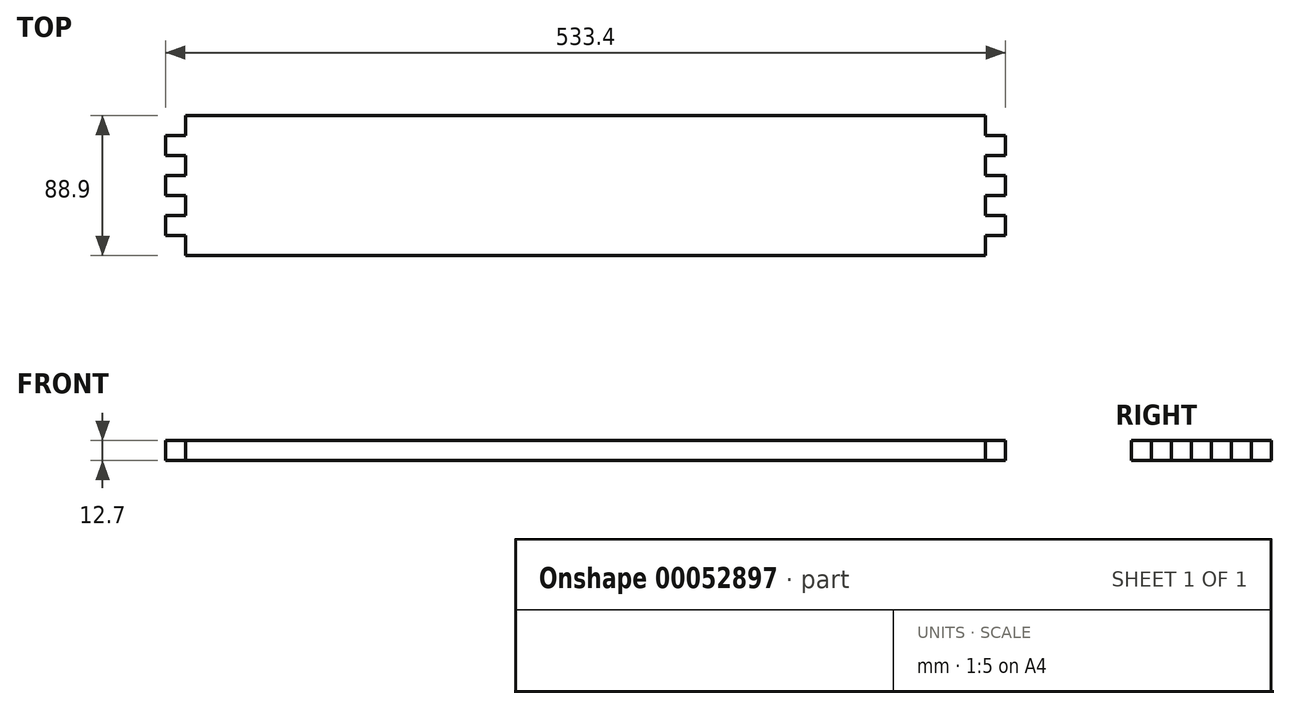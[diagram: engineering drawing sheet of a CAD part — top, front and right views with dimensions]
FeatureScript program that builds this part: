
annotation { "Feature Type Name" : "Feature", "Feature Type Description" : "" }
export const myFeature = defineFeature(function(context is Context, id is Id, definition is map)
    precondition{}
    {
        {
            var Q0;
            Q0=qCreatedBy(makeId("Top.planeOp"),FACE);
            var sketch = newSketch(context, id + "F0", { "sketchPlane" : qUnion([Q0])});
            skLineSegment(sketch, "E0.bottom", {"start": v(0, 0) * mm, "end": v(533.4, 0) * mm});
            skLineSegment(sketch, "E0.top", {"start": v(0, 88.9) * mm, "end": v(533.4, 88.9) * mm});
            skLineSegment(sketch, "E0.left", {"start": v(0, 0) * mm, "end": v(0, 88.9) * mm});
            skLineSegment(sketch, "E0.right", {"start": v(533.4, 0) * mm, "end": v(533.4, 88.9) * mm});
            skSolve(sketch);
        }
        {
            var Q0;
            Q0=qSketchRegion(id+"F0",true);
            extrude(context, id + "F1", {"entities" : qUnion([Q0]), "depth" : 12.7 * mm});
        }
        {
            var Q0;
            Q0=makeQuery(id+"F1.opExtrude","CAP_FACE",FACE,{"disambiguationData":[OSD([sQuery(id+"F0.wireOp",EDGE,"E0.bottom"),sQuery(id+"F0.wireOp",EDGE,"E0.top"),sQuery(id+"F0.wireOp",EDGE,"E0.left"),sQuery(id+"F0.wireOp",EDGE,"E0.right")])],"isStart":false});
            var sketch = newSketch(context, id + "F2", { "sketchPlane" : qUnion([Q0])});
            skLineSegment(sketch, "E1.bottom", {"start": v(533.4, 0) * mm, "end": v(520.7, 0) * mm});
            skLineSegment(sketch, "E1.top", {"start": v(533.4, 12.7) * mm, "end": v(520.7, 12.7) * mm});
            skLineSegment(sketch, "E1.left", {"start": v(533.4, 0) * mm, "end": v(533.4, 12.7) * mm});
            skLineSegment(sketch, "E1.right", {"start": v(520.7, 0) * mm, "end": v(520.7, 12.7) * mm});
            skLineSegment(sketch, "E2.bottom", {"start": v(533.4, 25.4) * mm, "end": v(520.7, 25.4) * mm});
            skLineSegment(sketch, "E2.top", {"start": v(533.4, 38.1) * mm, "end": v(520.7, 38.1) * mm});
            skLineSegment(sketch, "E2.left", {"start": v(533.4, 25.4) * mm, "end": v(533.4, 38.1) * mm});
            skLineSegment(sketch, "E2.right", {"start": v(520.7, 25.4) * mm, "end": v(520.7, 38.1) * mm});
            skLineSegment(sketch, "E3.bottom", {"start": v(533.4, 50.8) * mm, "end": v(520.7, 50.8) * mm});
            skLineSegment(sketch, "E3.top", {"start": v(533.4, 63.5) * mm, "end": v(520.7, 63.5) * mm});
            skLineSegment(sketch, "E3.left", {"start": v(533.4, 50.8) * mm, "end": v(533.4, 63.5) * mm});
            skLineSegment(sketch, "E3.right", {"start": v(520.7, 50.8) * mm, "end": v(520.7, 63.5) * mm});
            skLineSegment(sketch, "E4.bottom", {"start": v(533.4, 76.2) * mm, "end": v(520.7, 76.2) * mm});
            skLineSegment(sketch, "E4.top", {"start": v(533.4, 88.9) * mm, "end": v(520.7, 88.9) * mm});
            skLineSegment(sketch, "E4.left", {"start": v(533.4, 76.2) * mm, "end": v(533.4, 88.9) * mm});
            skLineSegment(sketch, "E4.right", {"start": v(520.7, 76.2) * mm, "end": v(520.7, 88.9) * mm});
            skSolve(sketch);
        }
        {
            var Q0;
            Q0=qSketchRegion(id+"F2",true);
            extrude(context, id + "F3", {"entities" : qUnion([Q0]), "operationType" : NewBodyOperationType.REMOVE, "oppositeDirection" : true, "depth" : 25.4 * mm});
        }
        {
            var Q0;
            Q0=makeQuery(id+"F1.opExtrude","CAP_FACE",FACE,{"disambiguationData":[OSD([sQuery(id+"F0.wireOp",EDGE,"E0.bottom"),sQuery(id+"F0.wireOp",EDGE,"E0.top"),sQuery(id+"F0.wireOp",EDGE,"E0.left"),sQuery(id+"F0.wireOp",EDGE,"E0.right")])],"isStart":false});
            var sketch = newSketch(context, id + "F4", { "sketchPlane" : qUnion([Q0])});
            skLineSegment(sketch, "E5.bottom", {"start": v(0, 0) * mm, "end": v(12.7, 0) * mm});
            skLineSegment(sketch, "E5.top", {"start": v(0, 12.7) * mm, "end": v(12.7, 12.7) * mm});
            skLineSegment(sketch, "E5.left", {"start": v(0, 0) * mm, "end": v(0, 12.7) * mm});
            skLineSegment(sketch, "E5.right", {"start": v(12.7, 0) * mm, "end": v(12.7, 12.7) * mm});
            skLineSegment(sketch, "E6.bottom", {"start": v(0, 25.4) * mm, "end": v(12.7, 25.4) * mm});
            skLineSegment(sketch, "E6.top", {"start": v(0, 38.1) * mm, "end": v(12.7, 38.1) * mm});
            skLineSegment(sketch, "E6.left", {"start": v(0, 25.4) * mm, "end": v(0, 38.1) * mm});
            skLineSegment(sketch, "E6.right", {"start": v(12.7, 25.4) * mm, "end": v(12.7, 38.1) * mm});
            skLineSegment(sketch, "E7.bottom", {"start": v(0, 76.2) * mm, "end": v(12.7, 76.2) * mm});
            skLineSegment(sketch, "E7.top", {"start": v(0, 88.9) * mm, "end": v(12.7, 88.9) * mm});
            skLineSegment(sketch, "E7.left", {"start": v(0, 76.2) * mm, "end": v(0, 88.9) * mm});
            skLineSegment(sketch, "E7.right", {"start": v(12.7, 76.2) * mm, "end": v(12.7, 88.9) * mm});
            skLineSegment(sketch, "E8.bottom", {"start": v(0, 50.8) * mm, "end": v(12.7, 50.8) * mm});
            skLineSegment(sketch, "E8.top", {"start": v(0, 63.5) * mm, "end": v(12.7, 63.5) * mm});
            skLineSegment(sketch, "E8.left", {"start": v(0, 50.8) * mm, "end": v(0, 63.5) * mm});
            skLineSegment(sketch, "E8.right", {"start": v(12.7, 50.8) * mm, "end": v(12.7, 63.5) * mm});
            skSolve(sketch);
        }
        {
            var Q0;
            Q0=qSketchRegion(id+"F4",true);
            extrude(context, id + "F5", {"entities" : qUnion([Q0]), "operationType" : NewBodyOperationType.REMOVE, "oppositeDirection" : true, "depth" : 25.4 * mm});
        }
    });
